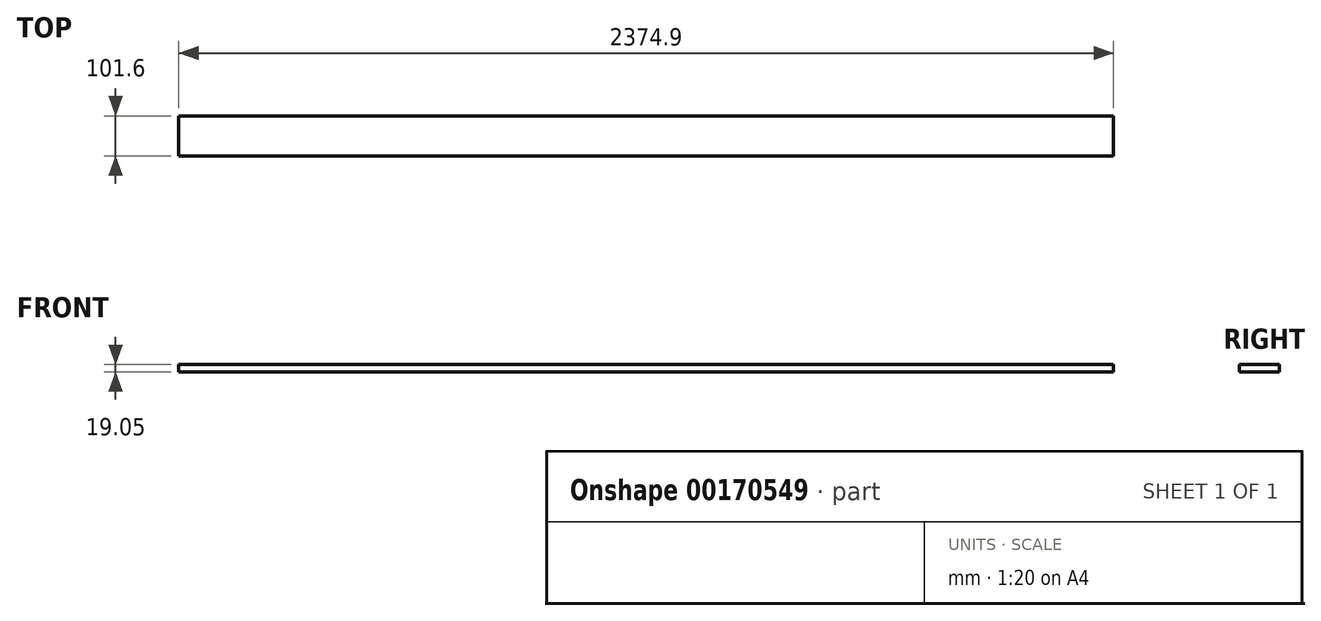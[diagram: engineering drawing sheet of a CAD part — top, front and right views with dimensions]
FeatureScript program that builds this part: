
annotation { "Feature Type Name" : "Feature", "Feature Type Description" : "" }
export const myFeature = defineFeature(function(context is Context, id is Id, definition is map)
    precondition{}
    {
        {
            var Q0;
            Q0=qCreatedBy(makeId("Top.planeOp"),FACE);
            var sketch = newSketch(context, id + "F0", { "sketchPlane" : qUnion([Q0])});
            skLineSegment(sketch, "E0.bottom", {"start": v(0, 0) * mm, "end": v(2374.9, 0) * mm});
            skLineSegment(sketch, "E0.top", {"start": v(0, 101.6) * mm, "end": v(2374.9, 101.6) * mm});
            skLineSegment(sketch, "E0.left", {"start": v(0, 0) * mm, "end": v(0, 101.6) * mm});
            skLineSegment(sketch, "E0.right", {"start": v(2374.9, 0) * mm, "end": v(2374.9, 101.6) * mm});
            skSolve(sketch);
        }
        {
            var Q0;
            Q0=makeQuery(id+"F0.imprint","IMPRINT",FACE,{"disambiguationData":[TD([[makeQuery(id+"F0.imprint","IMPRINT",EDGE,{"derivedFrom":sQuery(id+"F0.wireOp",EDGE,"E0.bottom")}),1.0]])]});
            extrude(context, id + "F1", {"entities" : qUnion([Q0]), "depth" : 19.05 * mm});
        }
    });
